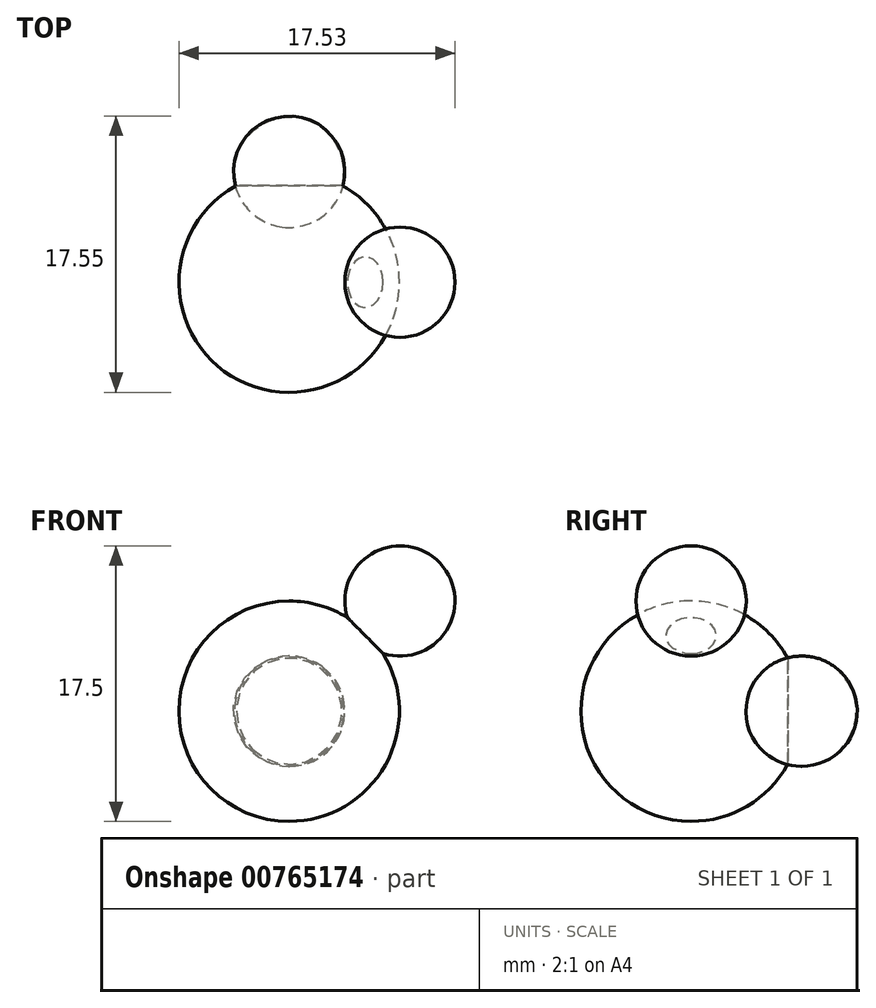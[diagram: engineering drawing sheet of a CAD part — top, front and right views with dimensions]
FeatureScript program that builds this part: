
annotation { "Feature Type Name" : "Feature", "Feature Type Description" : "" }
export const myFeature = defineFeature(function(context is Context, id is Id, definition is map)
    precondition{}
    {
        {
            var Q0;
            Q0=qCreatedBy(makeId("Front.planeOp"),FACE);
            var sketch = newSketch(context, id + "F0", { "sketchPlane" : qUnion([Q0])});
            skLineSegment(sketch, "E0", {"start": v(0, 0) * mm, "end": v(0, 7) * mm});
            skLineSegment(sketch, "E1", {"start": v(0, 0) * mm, "end": v(0, -7) * mm});
            skArc(sketch, "E2", {"start": v(0, -7) * mm, "mid": v(7, 0) * mm, "end": v(0, 7) * mm});
            skSolve(sketch);
        }
        {
            var Q0;
            Q0 = qSketchRegion(id + "F0", true);
            var Q1;
            Q1=sQuery(id+"F0.wireOp",EDGE,"E0");
            revolve(context, id + "F1", {"surfaceOperationType" : NewSurfaceOperationType.NEW, "entities" : qUnion([Q0]), "axis" : qUnion([Q1]), "revolveType" : RevolveType.FULL});
        }
        {
            var Q0;
            Q0=qCreatedBy(makeId("Front.planeOp"),FACE);
            var sketch = newSketch(context, id + "F2", { "sketchPlane" : qUnion([Q0])});
            skLineSegment(sketch, "E3", {"start": v(0, 6.9) * mm, "end": v(0, -7.06) * mm, "construction": true});
            skLineSegment(sketch, "E4", {"start": v(0, 0) * mm, "end": v(7.03, 0) * mm, "construction": true});
            skSolve(sketch);
        }
        {
            var Q0;
            Q0=sQuery(id+"F2.wireOp",VERTEX,"E4.end");
            var Q1;
            Q1=sQuery(id+"F2.wireOp",EDGE,"E4");
            cPlane(context, id + "F3", {"entities" : qUnion([Q0, Q1]), "cplaneType" : CPlaneType.LINE_POINT, "offset" : 25 * mm, "width" : 150 * mm, "height" : 150 * mm});
        }
        {
            var Q0;
            Q0=qCreatedBy(id+"F3.planeOp",FACE);
            var sketch = newSketch(context, id + "F4", { "sketchPlane" : qUnion([Q0])});
            skLineSegment(sketch, "E5", {"start": v(3.5, 7) * mm, "end": v(-3.5, 7) * mm});
            skArc(sketch, "E6", {"start": v(3.5, 7) * mm, "mid": v(0, 10.5) * mm, "end": v(-3.5, 7) * mm});
            skSolve(sketch);
        }
        {
            var Q0;
            Q0=makeQuery(id+"F4.imprint","IMPRINT",FACE,{"disambiguationData":[TD([[makeQuery(id+"F4.imprint","IMPRINT",EDGE,{"derivedFrom":sQuery(id+"F4.wireOp",EDGE,"E5")}),-1.0]])]});
            var Q1;
            Q1=sQuery(id+"F4.wireOp",EDGE,"E5");
            revolve(context, id + "F5", {"operationType" : NewBodyOperationType.ADD, "surfaceOperationType" : NewSurfaceOperationType.NEW, "entities" : qUnion([Q0]), "axis" : qUnion([Q1]), "revolveType" : RevolveType.FULL});
        }
        {
            var Q0;
            Q0=qCreatedBy(makeId("Right.planeOp"),FACE);
            var sketch = newSketch(context, id + "F6", { "sketchPlane" : qUnion([Q0])});
            skLineSegment(sketch, "E7", {"start": v(6.98, 0) * mm, "end": v(0, 0) * mm, "construction": true});
            skLineSegment(sketch, "E8", {"start": v(0, 0) * mm, "end": v(0, 6.89) * mm, "construction": true});
            skLineSegment(sketch, "E9", {"start": v(0, 6.89) * mm, "end": v(0, -6.9) * mm, "construction": true});
            skSolve(sketch);
        }
        {
            var Q0;
            Q0=qCreatedBy(makeId("Right.planeOp"),FACE);
            var sketch = newSketch(context, id + "F7", { "sketchPlane" : qUnion([Q0])});
            skLineSegment(sketch, "E10", {"start": v(7.01, 3.5) * mm, "end": v(7.01, -3.5) * mm});
            skArc(sketch, "E11", {"start": v(7.01, -3.5) * mm, "mid": v(10.48, 0) * mm, "end": v(7.01, 3.5) * mm});
            skSolve(sketch);
        }
        {
            var Q0;
            Q0=makeQuery(id+"F7.imprint","IMPRINT",FACE,{"disambiguationData":[TD([[makeQuery(id+"F7.imprint","IMPRINT",EDGE,{"derivedFrom":sQuery(id+"F7.wireOp",EDGE,"E10")}),1.0]])]});
            var Q1;
            Q1=sQuery(id+"F7.wireOp",EDGE,"E10");
            revolve(context, id + "F8", {"operationType" : NewBodyOperationType.ADD, "surfaceOperationType" : NewSurfaceOperationType.NEW, "entities" : qUnion([Q0]), "axis" : qUnion([Q1]), "revolveType" : RevolveType.FULL});
        }
    });
